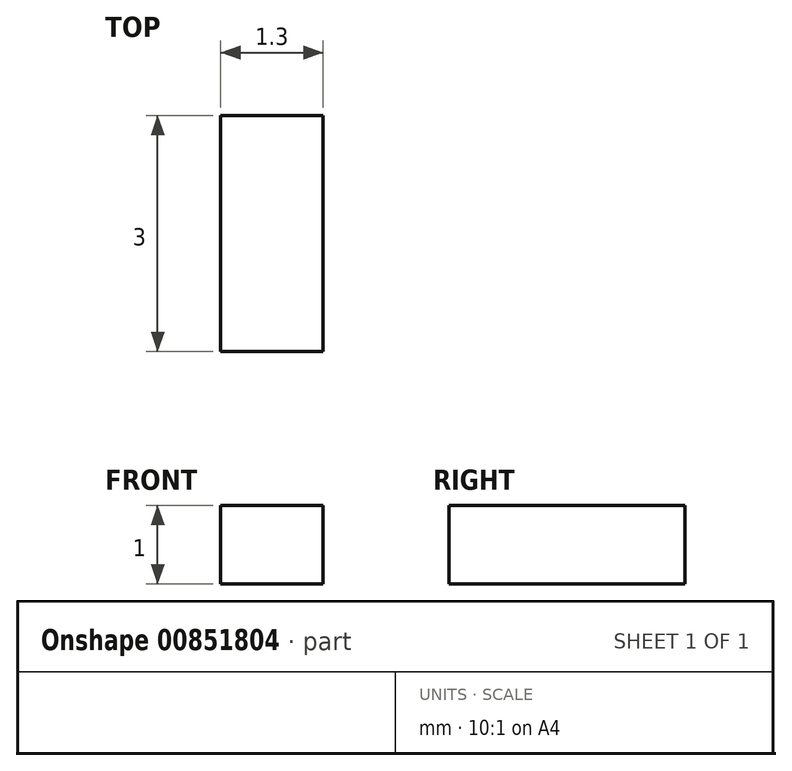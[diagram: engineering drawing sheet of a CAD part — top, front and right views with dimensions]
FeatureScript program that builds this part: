
annotation { "Feature Type Name" : "Feature", "Feature Type Description" : "" }
export const myFeature = defineFeature(function(context is Context, id is Id, definition is map)
    precondition{}
    {
        {
            var Q0;
            Q0=qCreatedBy(makeId("Front.planeOp"),FACE);
            var sketch = newSketch(context, id + "F0", { "sketchPlane" : qUnion([Q0])});
            skLineSegment(sketch, "E0.bottom", {"start": v(0.65, 0.5) * mm, "end": v(-0.65, 0.5) * mm});
            skLineSegment(sketch, "E0.top", {"start": v(0.65, -0.5) * mm, "end": v(-0.65, -0.5) * mm});
            skLineSegment(sketch, "E0.left", {"start": v(0.65, 0.5) * mm, "end": v(0.65, -0.5) * mm});
            skLineSegment(sketch, "E0.right", {"start": v(-0.65, 0.5) * mm, "end": v(-0.65, -0.5) * mm});
            skPoint(sketch, "E0.middle", {"position": v(0, 0) * mm});
            skSolve(sketch);
        }
        {
            var Q0;
            Q0=makeQuery(id+"F0.imprint","IMPRINT",FACE,{"disambiguationData":[TD([[makeQuery(id+"F0.imprint","IMPRINT",EDGE,{"derivedFrom":sQuery(id+"F0.wireOp",EDGE,"E0.bottom")}),1.0]])]});
            extrude(context, id + "F1", {"entities" : qUnion([Q0]), "depth" : 3 * mm, "offsetDistance" : 25.4 * mm});
        }
    });
